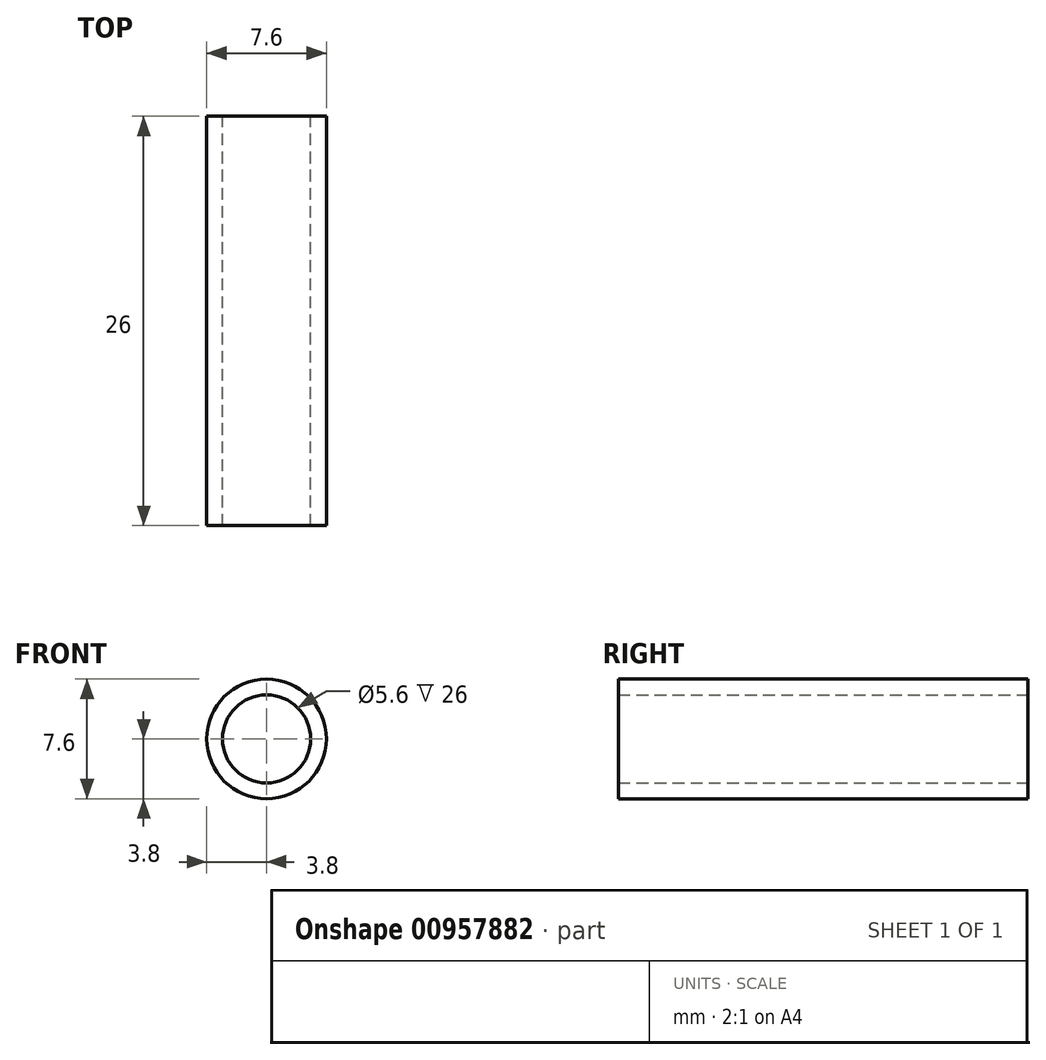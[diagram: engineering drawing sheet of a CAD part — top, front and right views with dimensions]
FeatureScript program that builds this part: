
annotation { "Feature Type Name" : "Feature", "Feature Type Description" : "" }
export const myFeature = defineFeature(function(context is Context, id is Id, definition is map)
    precondition{}
    {
        {
            var Q0;
            Q0=qCreatedBy(makeId("Front.planeOp"),FACE);
            var sketch = newSketch(context, id + "F0", { "sketchPlane" : qUnion([Q0])});
            skCircle(sketch, "E0", {"center": v(0, 0) * mm, "radius": 2.8 * mm});
            skCircle(sketch, "E1", {"center": v(0, 0) * mm, "radius": 3.8 * mm});
            skSolve(sketch);
        }
        {
            var Q0;
            Q0=makeQuery(id+"F0.imprint","IMPRINT",FACE,{"disambiguationData":[TD([[makeQuery(id+"F0.imprint","IMPRINT",EDGE,{"derivedFrom":sQuery(id+"F0.wireOp",EDGE,"E0")}),-1.0]])]});
            extrude(context, id + "F1", {"entities" : qUnion([Q0]), "depth" : 26 * mm, "offsetDistance" : 25 * mm});
        }
    });
